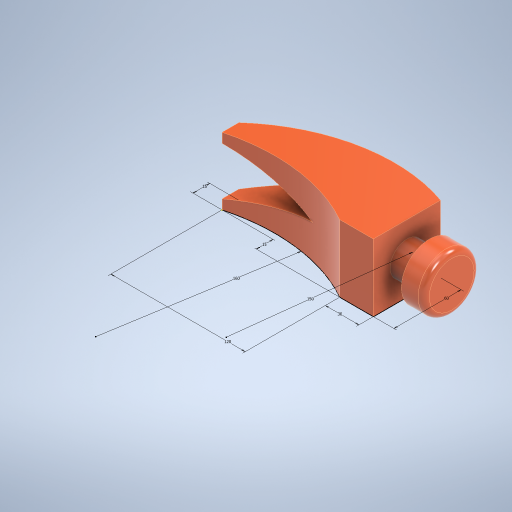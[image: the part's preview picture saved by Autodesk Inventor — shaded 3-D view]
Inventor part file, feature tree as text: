
AUTODESK INVENTOR PART (.ipt)
format: ipt  version: 2024 (Build 280153000, 153)  size: 314,880 bytes
history: native  units: mm
features: extrude x4, sketch x4, plane x1, fillet x1
ambient origin geometry x8: Origin, YZ Plane, XZ Plane, XY Plane, X Axis, Y Axis, Z Axis, Center Point
bodies: Volumenkörper1 (feature_tree)
feature tree (10):
  extrude  "Extrusion1"  Depth=15.0mm
  plane  "Arbeitsebene1"
  extrude  "Extrusion2"  TaperAngle=30.0deg  [1 undecoded]
  extrude  "Extrusion3"  Depth=60.0mm TaperAngle=0.0deg
  extrude  "Extrusion4"  Depth=20.0mm TaperAngle=0.0deg
  fillet  "Rundung1"  Radius=50.0mm
  sketch  "Skizze1"  dims[d12=120.0mm d14=15.0mm]
  sketch  "Skizze2"  dims[d15=60.0mm d16=0.0mm d17=30.0deg]
  sketch  "Skizze3"  dims[d18=80.0mm d19=60.0mm d20=0.0mm]
  sketch  "Skizze4"  dims[d21=30.0mm d22=20.0mm d23=0.0mm d24=50.0mm d25=20.0mm d26=0.0mm d27=5.0mm]
note: 1 required parameter value undecoded (feature->parameter linkage not recoverable at this tier; creation-order binding heuristic only, values carry confidence <= 0.55)
